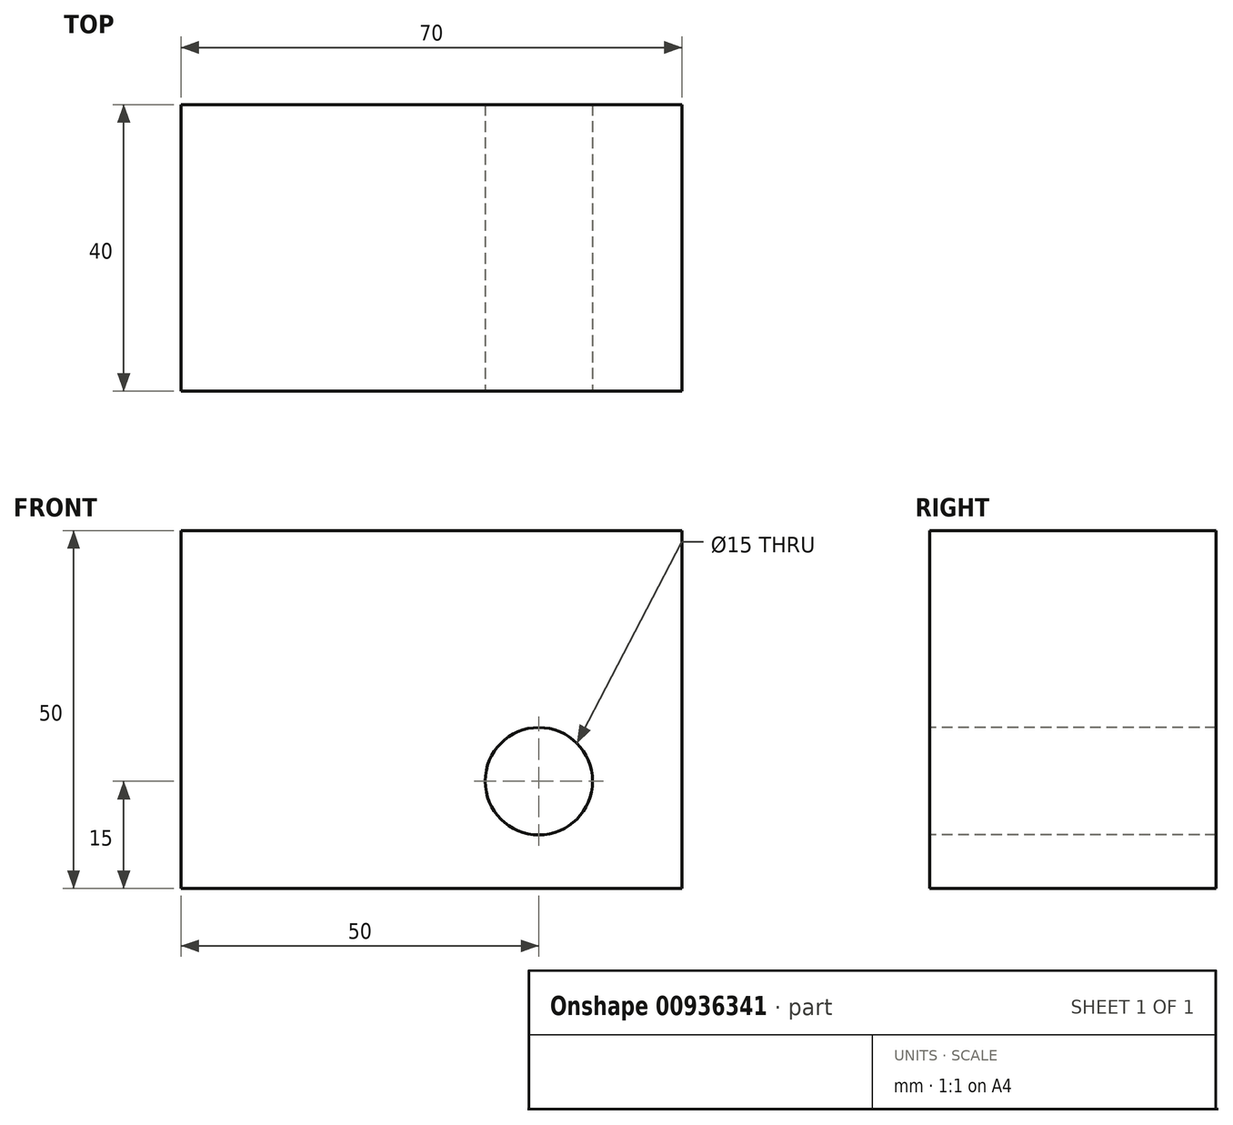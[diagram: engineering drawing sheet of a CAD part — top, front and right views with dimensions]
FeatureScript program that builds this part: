
annotation { "Feature Type Name" : "Feature", "Feature Type Description" : "" }
export const myFeature = defineFeature(function(context is Context, id is Id, definition is map)
    precondition{}
    {
        {
            var Q0;
            Q0=qCreatedBy(makeId("Front.planeOp"),FACE);
            var sketch = newSketch(context, id + "F0", { "sketchPlane" : qUnion([Q0])});
            skLineSegment(sketch, "E0.bottom", {"start": v(20, -15) * mm, "end": v(-50, -15) * mm});
            skLineSegment(sketch, "E0.top", {"start": v(20, 35) * mm, "end": v(-50, 35) * mm});
            skLineSegment(sketch, "E0.left", {"start": v(20, -15) * mm, "end": v(20, 35) * mm});
            skLineSegment(sketch, "E0.right", {"start": v(-50, -15) * mm, "end": v(-50, 35) * mm});
            skPoint(sketch, "E0.middle", {"position": v(-15, 10) * mm});
            skSolve(sketch);
        }
        {
            var Q0;
            Q0=makeQuery(id+"F0.imprint","IMPRINT",FACE,{"disambiguationData":[TD([[makeQuery(id+"F0.imprint","IMPRINT",EDGE,{"derivedFrom":sQuery(id+"F0.wireOp",EDGE,"E0.bottom")}),-1.0]])]});
            extrude(context, id + "F1", {"entities" : qUnion([Q0]), "depth" : 40 * mm, "offsetDistance" : 25 * mm, "symmetric" : true});
        }
        {
            var Q0;
            Q0=makeQuery(id+"F1.opExtrude","CAP_FACE",FACE,{"disambiguationData":[OSD([sQuery(id+"F0.wireOp",EDGE,"E0.bottom"),sQuery(id+"F0.wireOp",EDGE,"E0.top"),sQuery(id+"F0.wireOp",EDGE,"E0.left"),sQuery(id+"F0.wireOp",EDGE,"E0.right")])],"isStart":false});
            var sketch = newSketch(context, id + "F2", { "sketchPlane" : qUnion([Q0])});
            skCircle(sketch, "E1", {"center": v(0, 0) * mm, "radius": 7.5 * mm});
            skSolve(sketch);
        }
        {
            var Q0;
            Q0=makeQuery(id+"F2.imprint","IMPRINT",FACE,{"disambiguationData":[TD([[makeQuery(id+"F2.imprint","IMPRINT",EDGE,{"derivedFrom":sQuery(id+"F2.wireOp",EDGE,"E1")}),1.0]])]});
            var Q1;
            Q1=makeQuery(id+"F1.opExtrude","CAP_FACE",FACE,{"disambiguationData":[OSD([sQuery(id+"F0.wireOp",EDGE,"E0.bottom"),sQuery(id+"F0.wireOp",EDGE,"E0.top"),sQuery(id+"F0.wireOp",EDGE,"E0.left"),sQuery(id+"F0.wireOp",EDGE,"E0.right")])],"isStart":true});
            extrude(context, id + "F3", {"entities" : qUnion([Q0]), "operationType" : NewBodyOperationType.REMOVE, "endBound" : BoundingType.UP_TO_SURFACE, "oppositeDirection" : true, "depth" : 25 * mm, "endBoundEntityFace" : qUnion([Q1]), "offsetDistance" : 25 * mm});
        }
    });
